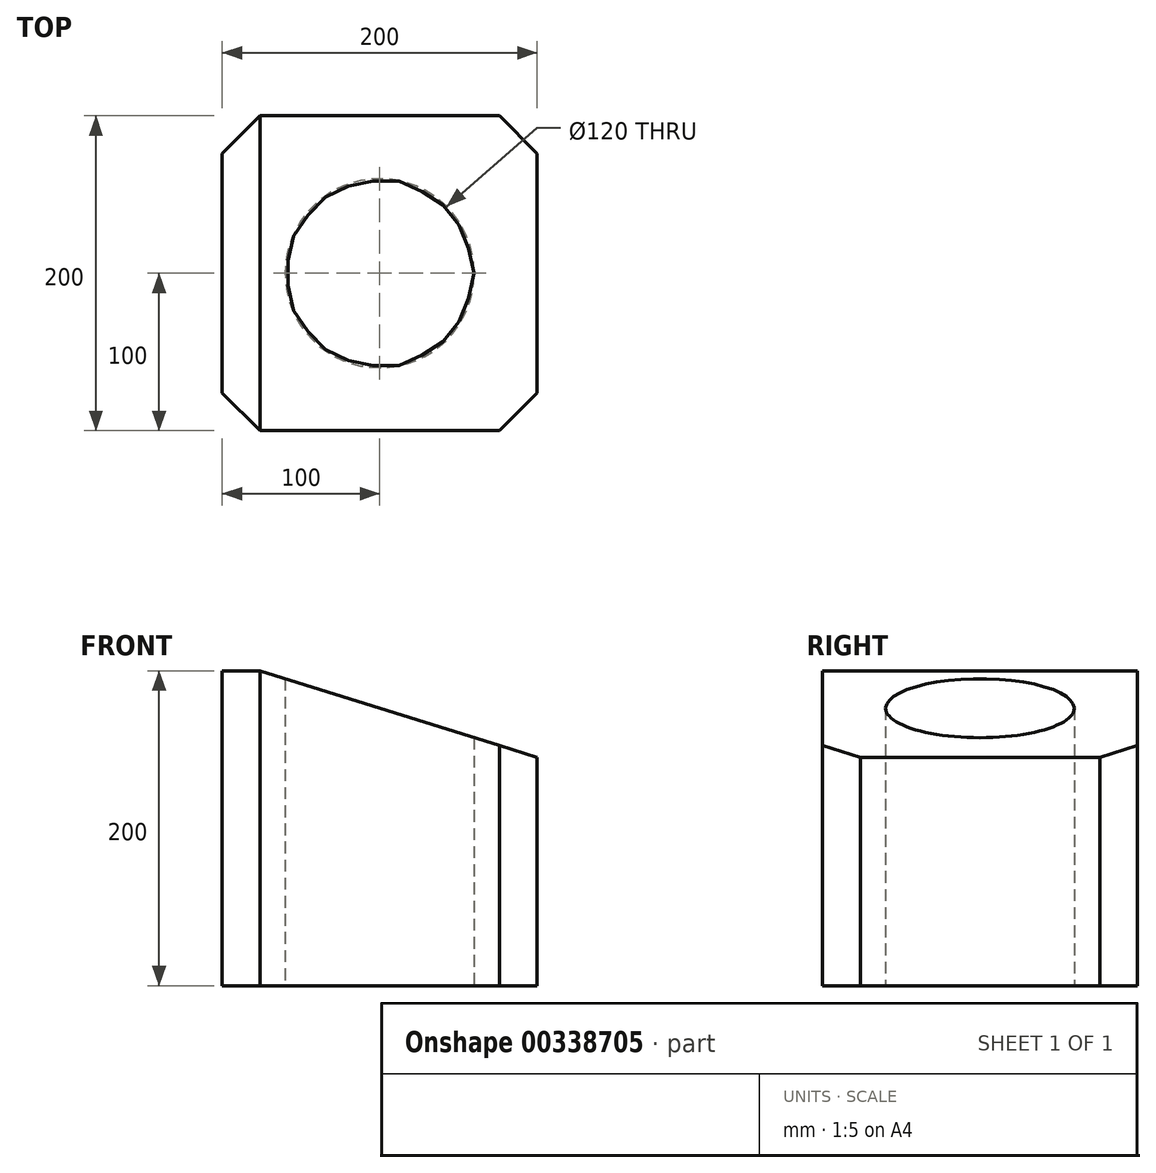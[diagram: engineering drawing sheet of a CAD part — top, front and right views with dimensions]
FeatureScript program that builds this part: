
annotation { "Feature Type Name" : "Feature", "Feature Type Description" : "" }
export const myFeature = defineFeature(function(context is Context, id is Id, definition is map)
    precondition{}
    {
        {
            var Q0;
            Q0=qCreatedBy(makeId("Top.planeOp"),FACE);
            var sketch = newSketch(context, id + "F0", { "sketchPlane" : qUnion([Q0])});
            skCircle(sketch, "E0", {"center": v(0, 0) * mm, "radius": 60 * mm});
            skLineSegment(sketch, "E1.bottom", {"start": v(-100, 100) * mm, "end": v(100, 100) * mm});
            skLineSegment(sketch, "E1.top", {"start": v(-100, -100) * mm, "end": v(100, -100) * mm});
            skLineSegment(sketch, "E1.left", {"start": v(-100, 100) * mm, "end": v(-100, -100) * mm});
            skLineSegment(sketch, "E1.right", {"start": v(100, 100) * mm, "end": v(100, -100) * mm});
            skSolve(sketch);
        }
        {
            var Q0;
            Q0=makeQuery(id+"F0.imprint","IMPRINT",FACE,{"disambiguationData":[TD([[makeQuery(id+"F0.imprint","IMPRINT",EDGE,{"derivedFrom":sQuery(id+"F0.wireOp",EDGE,"E0")}),-1.0]])]});
            extrude(context, id + "F1", {"entities" : qUnion([Q0]), "endBound" : BoundingType.SYMMETRIC, "depth" : 200 * mm});
        }
        {
            var Q0;
            Q0=makeQuery(id+"F1.opExtrude","SWEPT_EDGE",EDGE,{"disambiguationData":[OSD([sQuery(id+"F0.wireOp",EDGE,"E1.top"),sQuery(id+"F0.wireOp",EDGE,"E1.left")])]});
            var Q1;
            Q1=makeQuery(id+"F1.opExtrude","SWEPT_EDGE",EDGE,{"disambiguationData":[OSD([sQuery(id+"F0.wireOp",EDGE,"E1.top"),sQuery(id+"F0.wireOp",EDGE,"E1.right")])]});
            var Q2;
            Q2=makeQuery(id+"F1.opExtrude","SWEPT_EDGE",EDGE,{"disambiguationData":[OSD([sQuery(id+"F0.wireOp",EDGE,"E1.bottom"),sQuery(id+"F0.wireOp",EDGE,"E1.right")])]});
            var Q3;
            Q3=makeQuery(id+"F1.opExtrude","SWEPT_EDGE",EDGE,{"disambiguationData":[OSD([sQuery(id+"F0.wireOp",EDGE,"E1.bottom"),sQuery(id+"F0.wireOp",EDGE,"E1.left")])]});
            chamfer(context, id + "F2", {"entities" : qUnion([Q0, Q1, Q2, Q3]), "width" : 24 * mm, "tangentPropagation" : true});
        }
        {
            var Q0;
            Q0=makeQuery(id+"F1.opExtrude","SWEPT_FACE",FACE,{"disambiguationData":[OSD([sQuery(id+"F0.wireOp",EDGE,"E1.top")])]});
            var sketch = newSketch(context, id + "F3", { "sketchPlane" : qUnion([Q0])});
            skLineSegment(sketch, "E2.0", {"start": v(100, 100) * mm, "end": v(100, 45) * mm});
            skLineSegment(sketch, "E3", {"start": v(-76, 100) * mm, "end": v(100, 100) * mm});
            skLineSegment(sketch, "E4", {"start": v(-76, 100) * mm, "end": v(100, 45) * mm});
            skPoint(sketch, "E5.0.end.orphan", {"position": v(-100, 100) * mm});
            skPoint(sketch, "E5.0.start.orphan", {"position": v(-100, -100) * mm});
            skPoint(sketch, "E6.orphan", {"position": v(100, -100) * mm});
            skPoint(sketch, "E7.0.end.orphan", {"position": v(-76, -100) * mm});
            skSolve(sketch);
        }
        {
            var Q0;
            Q0 = qSketchRegion(id + "F3", true);
            extrude(context, id + "F4", {"entities" : qUnion([Q0]), "operationType" : NewBodyOperationType.REMOVE, "oppositeDirection" : true, "depth" : 200 * mm});
        }
    });
